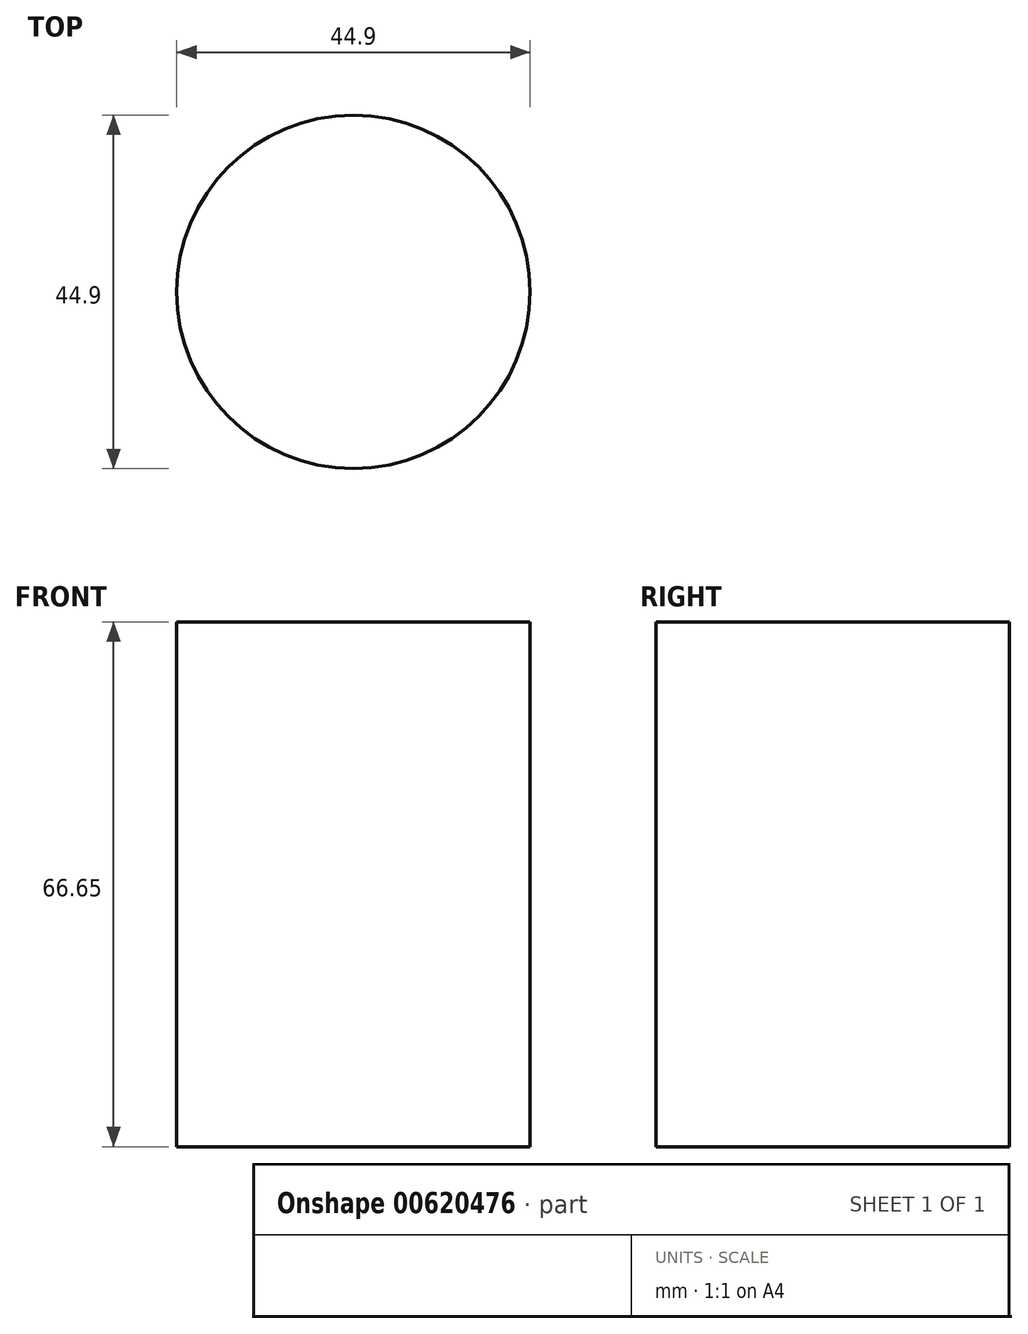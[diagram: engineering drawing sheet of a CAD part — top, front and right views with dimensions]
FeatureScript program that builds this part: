
annotation { "Feature Type Name" : "Feature", "Feature Type Description" : "" }
export const myFeature = defineFeature(function(context is Context, id is Id, definition is map)
    precondition{}
    {
        {
            var Q0;
            Q0=qCreatedBy(makeId("Front.planeOp"),FACE);
            var sketch = newSketch(context, id + "F0", { "sketchPlane" : qUnion([Q0])});
            skLineSegment(sketch, "E0.bottom", {"start": v(0, 74.24) * mm, "end": v(-43.96, 74.24) * mm});
            skLineSegment(sketch, "E0.top", {"start": v(0, 55.95) * mm, "end": v(-43.96, 55.95) * mm});
            skLineSegment(sketch, "E0.left", {"start": v(0, 74.24) * mm, "end": v(0, 55.95) * mm});
            skLineSegment(sketch, "E0.right", {"start": v(-43.96, 74.24) * mm, "end": v(-43.96, 55.95) * mm});
            skLineSegment(sketch, "E1.bottom", {"start": v(0, 55.95) * mm, "end": v(-34.82, 55.95) * mm});
            skLineSegment(sketch, "E1.top", {"start": v(0, 38.48) * mm, "end": v(-34.82, 38.48) * mm});
            skLineSegment(sketch, "E1.left", {"start": v(0, 55.95) * mm, "end": v(0, 38.48) * mm});
            skLineSegment(sketch, "E1.right", {"start": v(-34.82, 55.95) * mm, "end": v(-34.82, 38.48) * mm});
            skLineSegment(sketch, "E2.bottom", {"start": v(0, 38.48) * mm, "end": v(-28.9, 38.48) * mm});
            skLineSegment(sketch, "E2.top", {"start": v(0, 20.73) * mm, "end": v(-28.9, 20.73) * mm});
            skLineSegment(sketch, "E2.left", {"start": v(0, 38.48) * mm, "end": v(0, 20.73) * mm});
            skLineSegment(sketch, "E2.right", {"start": v(-28.9, 38.48) * mm, "end": v(-28.9, 20.73) * mm});
            skLineSegment(sketch, "E3.bottom", {"start": v(0, 20.73) * mm, "end": v(-21.1, 20.73) * mm});
            skLineSegment(sketch, "E3.top", {"start": v(0, 9.98) * mm, "end": v(-21.1, 9.98) * mm});
            skLineSegment(sketch, "E3.left", {"start": v(0, 20.73) * mm, "end": v(0, 9.98) * mm});
            skLineSegment(sketch, "E3.right", {"start": v(-21.1, 20.73) * mm, "end": v(-21.1, 9.98) * mm});
            skLineSegment(sketch, "E4.bottom", {"start": v(0, 9.98) * mm, "end": v(-15.2, 9.98) * mm});
            skLineSegment(sketch, "E4.top", {"start": v(0, 0) * mm, "end": v(-15.2, 0) * mm});
            skLineSegment(sketch, "E4.left", {"start": v(0, 9.98) * mm, "end": v(0, 0) * mm});
            skLineSegment(sketch, "E4.right", {"start": v(-15.2, 9.98) * mm, "end": v(-15.2, 0) * mm});
            skLineSegment(sketch, "E5.bottom", {"start": v(0, 0) * mm, "end": v(-22.45, 0) * mm});
            skLineSegment(sketch, "E5.top", {"start": v(0, -66.65) * mm, "end": v(-22.45, -66.65) * mm});
            skLineSegment(sketch, "E5.left", {"start": v(0, 0) * mm, "end": v(0, -66.65) * mm});
            skLineSegment(sketch, "E5.right", {"start": v(-22.45, 0) * mm, "end": v(-22.45, -66.65) * mm});
            skLineSegment(sketch, "E6.bottom", {"start": v(0, -66.65) * mm, "end": v(-16.27, -66.65) * mm});
            skLineSegment(sketch, "E6.top", {"start": v(0, -70.42) * mm, "end": v(-16.27, -70.42) * mm});
            skLineSegment(sketch, "E6.left", {"start": v(0, -66.65) * mm, "end": v(0, -70.42) * mm});
            skLineSegment(sketch, "E6.right", {"start": v(-16.27, -66.65) * mm, "end": v(-16.27, -70.42) * mm});
            skLineSegment(sketch, "E7.bottom", {"start": v(0, -70.42) * mm, "end": v(-41.8, -70.42) * mm});
            skLineSegment(sketch, "E7.top", {"start": v(0, -77.95) * mm, "end": v(-41.8, -77.95) * mm});
            skLineSegment(sketch, "E7.left", {"start": v(0, -70.42) * mm, "end": v(0, -77.95) * mm});
            skLineSegment(sketch, "E7.right", {"start": v(-41.8, -70.42) * mm, "end": v(-41.8, -77.95) * mm});
            skPoint(sketch, "E8.oppositeSnap0", {"position": v(-41.8, -74.18) * mm});
            skLineSegment(sketch, "E8.bottom", {"start": v(-41.8, -74.18) * mm, "end": v(-35.09, -74.18) * mm});
            skLineSegment(sketch, "E8.top", {"start": v(-41.8, -74.18) * mm, "end": v(-35.09, -74.18) * mm});
            skLineSegment(sketch, "E8.left", {"start": v(-41.8, -74.18) * mm, "end": v(-41.8, -74.18) * mm});
            skLineSegment(sketch, "E8.right", {"start": v(-35.09, -74.18) * mm, "end": v(-35.09, -74.18) * mm});
            skSolve(sketch);
        }
        {
            var Q0;
            Q0=makeQuery(id+"F0.imprint","IMPRINT",FACE,{"disambiguationData":[TD([[makeQuery(id+"F0.imprint","IMPRINT",EDGE,{"derivedFrom":sQuery(id+"F0.wireOp",EDGE,"E1.bottom")}),1.0]])]});
            var Q1;
            Q1=makeQuery(id+"F0.imprint","IMPRINT",FACE,{"disambiguationData":[TD([[makeQuery(id+"F0.imprint","IMPRINT",EDGE,{"derivedFrom":sQuery(id+"F0.wireOp",EDGE,"E2.bottom")}),1.0]])]});
            var Q2;
            Q2=makeQuery(id+"F0.imprint","IMPRINT",FACE,{"disambiguationData":[TD([[makeQuery(id+"F0.imprint","IMPRINT",EDGE,{"derivedFrom":sQuery(id+"F0.wireOp",EDGE,"E6.bottom")}),1.0]])]});
            var Q3;
            Q3=makeQuery(id+"F0.imprint","IMPRINT",FACE,{"disambiguationData":[TD([[makeQuery(id+"F0.imprint","IMPRINT",EDGE,{"derivedFrom":sQuery(id+"F0.wireOp",EDGE,"E5.top")}),-1.0]])]});
            var Q4;
            Q4=makeQuery(id+"F0.imprint","IMPRINT",FACE,{"disambiguationData":[TD([[makeQuery(id+"F0.imprint","IMPRINT",EDGE,{"derivedFrom":sQuery(id+"F0.wireOp",EDGE,"E4.bottom")}),1.0]])]});
            var Q5;
            Q5=makeQuery(id+"F0.imprint","IMPRINT",FACE,{"disambiguationData":[TD([[makeQuery(id+"F0.imprint","IMPRINT",EDGE,{"derivedFrom":sQuery(id+"F0.wireOp",EDGE,"E3.bottom")}),1.0]])]});
            var Q6;
            Q6=sQuery(id+"F0.wireOp",EDGE,"E7.left");
            revolve(context, id + "F1", {"entities" : qUnion([Q0, Q1, Q2, Q3, Q4, Q5]), "axis" : qUnion([Q6]), "revolveType" : RevolveType.FULL});
        }
    });
